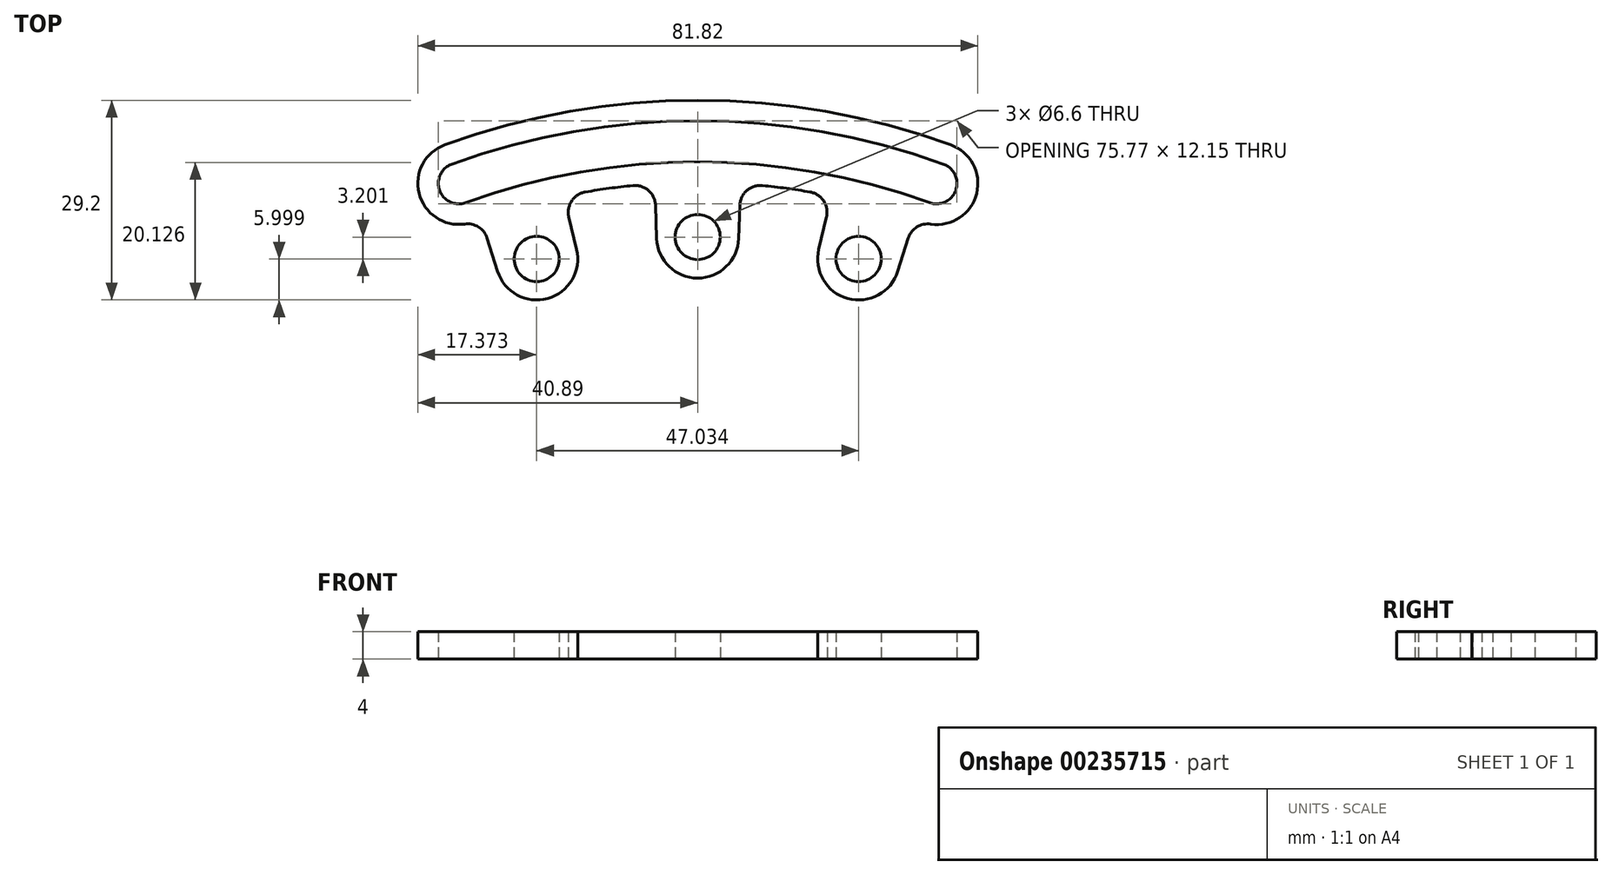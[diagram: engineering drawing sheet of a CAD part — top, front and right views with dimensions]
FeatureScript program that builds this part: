
annotation { "Feature Type Name" : "Feature", "Feature Type Description" : "" }
export const myFeature = defineFeature(function(context is Context, id is Id, definition is map)
    precondition{}
    {
        {
            var Q0;
            Q0=qCreatedBy(makeId("Top.planeOp"),FACE);
            var sketch = newSketch(context, id + "F0", { "sketchPlane" : qUnion([Q0])});
            skArc(sketch, "E0", {"start": v(36.94, 101.49) * mm, "mid": v(0, 108) * mm, "end": v(-36.94, 101.49) * mm});
            skLineSegment(sketch, "E1", {"start": v(0, 0) * mm, "end": v(0, 108) * mm, "construction": true});
            skLineSegment(sketch, "E2", {"start": v(0, 0) * mm, "end": v(-36.94, 101.49) * mm, "construction": true});
            skArc(sketch, "E3.0", {"start": v(35.91, 98.67) * mm, "mid": v(0, 105) * mm, "end": v(-35.91, 98.67) * mm});
            skArc(sketch, "E4.0", {"start": v(33.86, 93.03) * mm, "mid": v(0, 99) * mm, "end": v(-33.86, 93.03) * mm});
            skArc(sketch, "E5.0", {"start": v(-9.46, 95.53) * mm, "mid": v(-12.95, 95.12) * mm, "end": v(-16.42, 94.59) * mm});
            skArc(sketch, "E6", {"start": v(-36.94, 101.49) * mm, "mid": v(-40.7, 94.4) * mm, "end": v(-34.04, 89.9) * mm});
            skArc(sketch, "E7", {"start": v(-35.91, 98.67) * mm, "mid": v(-37.7, 94.82) * mm, "end": v(-33.86, 93.03) * mm});
            skArc(sketch, "E8.0", {"start": v(30.1, 82.7) * mm, "mid": v(0, 88) * mm, "end": v(-30.1, 82.7) * mm, "construction": true});
            skLineSegment(sketch, "E9", {"start": v(0, 0) * mm, "end": v(23.52, 84.8) * mm, "construction": true});
            skLineSegment(sketch, "E10", {"start": v(0, 0) * mm, "end": v(36.94, 101.49) * mm, "construction": true});
            skArc(sketch, "E11", {"start": v(33.86, 93.03) * mm, "mid": v(37.7, 94.82) * mm, "end": v(35.91, 98.67) * mm});
            skArc(sketch, "E12", {"start": v(34.06, 89.9) * mm, "mid": v(40.75, 94.39) * mm, "end": v(36.94, 101.49) * mm});
            skLineSegment(sketch, "E13", {"start": v(0, 0) * mm, "end": v(-23.52, 84.8) * mm, "construction": true});
            skCircle(sketch, "E14", {"center": v(-23.52, 84.8) * mm, "radius": 6 * mm});
            skCircle(sketch, "E15", {"center": v(0, 88) * mm, "radius": 6 * mm});
            skCircle(sketch, "E16", {"center": v(23.52, 84.8) * mm, "radius": 6 * mm});
            skLineSegment(sketch, "E17", {"start": v(-6, 87.8) * mm, "end": v(-6.16, 92.65) * mm});
            skLineSegment(sketch, "E18", {"start": v(6, 87.8) * mm, "end": v(6.16, 92.65) * mm});
            skLineSegment(sketch, "E19", {"start": v(-29.24, 83) * mm, "end": v(-30.76, 87.84) * mm});
            skLineSegment(sketch, "E20", {"start": v(-17.68, 86.2) * mm, "end": v(-18.82, 90.93) * mm});
            skLineSegment(sketch, "E21", {"start": v(17.68, 86.2) * mm, "end": v(18.82, 90.93) * mm});
            skLineSegment(sketch, "E22", {"start": v(29.24, 83) * mm, "end": v(30.76, 87.83) * mm});
            skArc(sketch, "E23.filletArc", {"start": v(-6.16, 92.65) * mm, "mid": v(-7.18, 94.8) * mm, "end": v(-9.46, 95.53) * mm});
            skArc(sketch, "E24.filletArc", {"start": v(-16.42, 94.59) * mm, "mid": v(-18.41, 93.28) * mm, "end": v(-18.82, 90.93) * mm});
            skArc(sketch, "E25", {"start": v(16.42, 94.59) * mm, "mid": v(12.95, 95.12) * mm, "end": v(9.46, 95.53) * mm});
            skPoint(sketch, "E26.visualSharp", {"position": v(6.27, 95.8) * mm});
            skArc(sketch, "E26.filletArc", {"start": v(9.46, 95.53) * mm, "mid": v(7.18, 94.8) * mm, "end": v(6.16, 92.65) * mm});
            skPoint(sketch, "E27.visualSharp", {"position": v(19.56, 93.99) * mm});
            skArc(sketch, "E27.filletArc", {"start": v(18.82, 90.93) * mm, "mid": v(18.41, 93.28) * mm, "end": v(16.42, 94.59) * mm});
            skArc(sketch, "E28", {"start": v(-30.76, 87.84) * mm, "mid": v(-32.02, 89.48) * mm, "end": v(-34.04, 89.9) * mm});
            skArc(sketch, "E29", {"start": v(34.06, 89.9) * mm, "mid": v(32.03, 89.47) * mm, "end": v(30.76, 87.83) * mm});
            skCircle(sketch, "E30", {"center": v(-23.52, 84.8) * mm, "radius": 3.3 * mm});
            skCircle(sketch, "E31", {"center": v(0, 88) * mm, "radius": 3.3 * mm});
            skCircle(sketch, "E32", {"center": v(23.52, 84.8) * mm, "radius": 3.3 * mm});
            skSolve(sketch);
        }
        {
            var Q0;
            Q0=makeQuery(id+"F0.imprint","IMPRINT",FACE,{"disambiguationData":[TD([[makeQuery(id+"F0.imprint","IMPRINT",EDGE,{"derivedFrom":sQuery(id+"F0.wireOp",EDGE,"E31")}),1.0]])]});
            var Q1;
            Q1=makeQuery(id+"F0.imprint","IMPRINT",FACE,{"disambiguationData":[TD([[makeQuery(id+"F0.imprint","IMPRINT",EDGE,{"derivedFrom":sQuery(id+"F0.wireOp",EDGE,"E31")}),-1.0]])]});
            var Q2;
            Q2=makeQuery(id+"F0.imprint","IMPRINT",FACE,{"disambiguationData":[TD([[makeQuery(id+"F0.imprint","IMPRINT",EDGE,{"derivedFrom":sQuery(id+"F0.wireOp",EDGE,"E32")}),1.0]])]});
            var Q3;
            Q3=makeQuery(id+"F0.imprint","IMPRINT",FACE,{"disambiguationData":[TD([[makeQuery(id+"F0.imprint","IMPRINT",EDGE,{"derivedFrom":sQuery(id+"F0.wireOp",EDGE,"E32")}),-1.0]])]});
            var Q4;
            Q4=makeQuery(id+"F0.imprint","IMPRINT",FACE,{"disambiguationData":[TD([[makeQuery(id+"F0.imprint","IMPRINT",EDGE,{"derivedFrom":sQuery(id+"F0.wireOp",EDGE,"E30")}),1.0]])]});
            var Q5;
            Q5=makeQuery(id+"F0.imprint","IMPRINT",FACE,{"disambiguationData":[TD([[makeQuery(id+"F0.imprint","IMPRINT",EDGE,{"derivedFrom":sQuery(id+"F0.wireOp",EDGE,"E30")}),-1.0]])]});
            var Q6;
            Q6=makeQuery(id+"F0.imprint","IMPRINT",FACE,{"disambiguationData":[TD([[makeQuery(id+"F0.imprint","IMPRINT",EDGE,{"derivedFrom":sQuery(id+"F0.wireOp",EDGE,"E0")}),1.0]])]});
            extrude(context, id + "F1", {"entities" : qUnion([Q0, Q1, Q2, Q3, Q4, Q5, Q6]), "depth" : 4 * mm});
        }
        {
            var Q0;
            Q0=sQuery(id+"F0.wireOp",VERTEX,"E14.center");
            var Q1;
            Q1=sQuery(id+"F0.wireOp",VERTEX,"E31.center");
            var Q2;
            Q2=sQuery(id+"F0.wireOp",VERTEX,"E16.center");
            var Q3;
            Q3=makeQuery(id+"F1.opExtrude","SWEPT_BODY",BODY,{"disambiguationData":[OSD([sQuery(id+"F0.wireOp",EDGE,"E0"),sQuery(id+"F0.wireOp",EDGE,"E5.0"),sQuery(id+"F0.wireOp",EDGE,"E6"),sQuery(id+"F0.wireOp",EDGE,"E12"),sQuery(id+"F0.wireOp",EDGE,"E14"),sQuery(id+"F0.wireOp",EDGE,"E15"),sQuery(id+"F0.wireOp",EDGE,"E16"),sQuery(id+"F0.wireOp",EDGE,"E17"),sQuery(id+"F0.wireOp",EDGE,"E18"),sQuery(id+"F0.wireOp",EDGE,"E19"),sQuery(id+"F0.wireOp",EDGE,"E20"),sQuery(id+"F0.wireOp",EDGE,"E21"),sQuery(id+"F0.wireOp",EDGE,"E22"),sQuery(id+"F0.wireOp",EDGE,"E23.filletArc"),sQuery(id+"F0.wireOp",EDGE,"E24.filletArc"),sQuery(id+"F0.wireOp",EDGE,"E25"),sQuery(id+"F0.wireOp",EDGE,"E26.filletArc"),sQuery(id+"F0.wireOp",EDGE,"E27.filletArc"),sQuery(id+"F0.wireOp",EDGE,"E28"),sQuery(id+"F0.wireOp",EDGE,"E29")])]});
            hole(context, id + "F2", {"style" : HoleStyle.SIMPLE, "endStyle" : HoleEndStyle.THROUGH, "oppositeDirection" : true, "holeDiameter" : 6.6 * mm, "locations" : qUnion([Q0, Q1, Q2]), "scope" : qUnion([Q3]), "isTappedThrough" : true});
        }
    });
